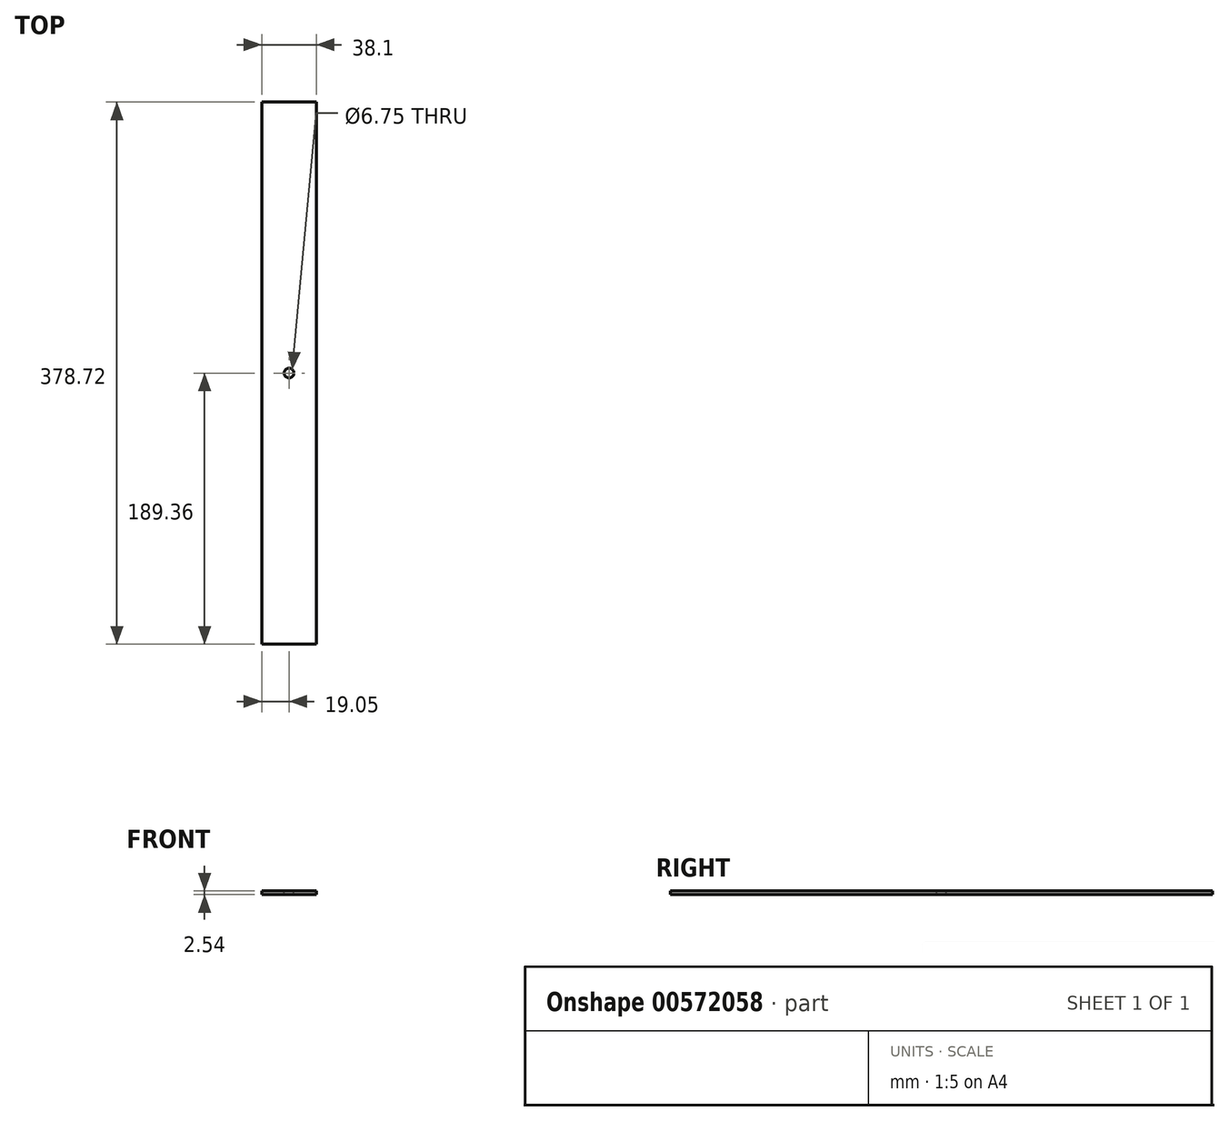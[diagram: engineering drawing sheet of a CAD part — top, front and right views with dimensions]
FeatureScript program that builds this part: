
annotation { "Feature Type Name" : "Feature", "Feature Type Description" : "" }
export const myFeature = defineFeature(function(context is Context, id is Id, definition is map)
    precondition{}
    {
        {
            var Q0;
            Q0=qCreatedBy(makeId("Top.planeOp"),FACE);
            var sketch = newSketch(context, id + "F0", { "sketchPlane" : qUnion([Q0])});
            skLineSegment(sketch, "E0.bottom", {"start": v(15.37, 189.36) * mm, "end": v(-22.73, 189.36) * mm});
            skLineSegment(sketch, "E0.top", {"start": v(15.37, -189.36) * mm, "end": v(-22.73, -189.36) * mm});
            skLineSegment(sketch, "E0.left", {"start": v(15.37, 189.36) * mm, "end": v(15.37, -189.36) * mm});
            skLineSegment(sketch, "E0.right", {"start": v(-22.73, 189.36) * mm, "end": v(-22.73, -189.36) * mm});
            skPoint(sketch, "E0.middle", {"position": v(-3.68, 0) * mm});
            skSolve(sketch);
        }
        {
            var Q0;
            Q0=makeQuery(id+"F0.imprint","IMPRINT",FACE,{"disambiguationData":[TD([[makeQuery(id+"F0.imprint","IMPRINT",EDGE,{"derivedFrom":sQuery(id+"F0.wireOp",EDGE,"E0.bottom")}),1.0]])]});
            extrude(context, id + "F1", {"entities" : qUnion([Q0]), "depth" : 2.54 * mm, "offsetDistance" : 25.4 * mm});
        }
        {
            var Q0;
            Q0=makeQuery(id+"F1.opExtrude","CAP_FACE",FACE,{"disambiguationData":[OSD([sQuery(id+"F0.wireOp",EDGE,"E0.bottom"),sQuery(id+"F0.wireOp",EDGE,"E0.top"),sQuery(id+"F0.wireOp",EDGE,"E0.left"),sQuery(id+"F0.wireOp",EDGE,"E0.right")])],"isStart":false});
            var sketch = newSketch(context, id + "F2", { "sketchPlane" : qUnion([Q0])});
            skPoint(sketch, "E1", {"position": v(-3.68, 0) * mm});
            skSolve(sketch);
        }
        {
            var Q0;
            Q0=sQuery(id+"F2.wireOp",VERTEX,"E1");
            var Q1;
            Q1=makeQuery(id+"F1.opExtrude","SWEPT_BODY",BODY,{"disambiguationData":[OSD([sQuery(id+"F0.wireOp",EDGE,"E0.bottom"),sQuery(id+"F0.wireOp",EDGE,"E0.top"),sQuery(id+"F0.wireOp",EDGE,"E0.left"),sQuery(id+"F0.wireOp",EDGE,"E0.right")])]});
            hole(context, id + "F3", {"style" : HoleStyle.SIMPLE, "endStyle" : HoleEndStyle.THROUGH, "holeDiameter" : 6.75 * mm, "majorDiameter" : 6.35 * mm, "isTappedThrough" : true, "tappedDepth" : 12.7 * mm, "tapClearance" : 3, "locations" : qUnion([Q0]), "scope" : qUnion([Q1])});
        }
    });
